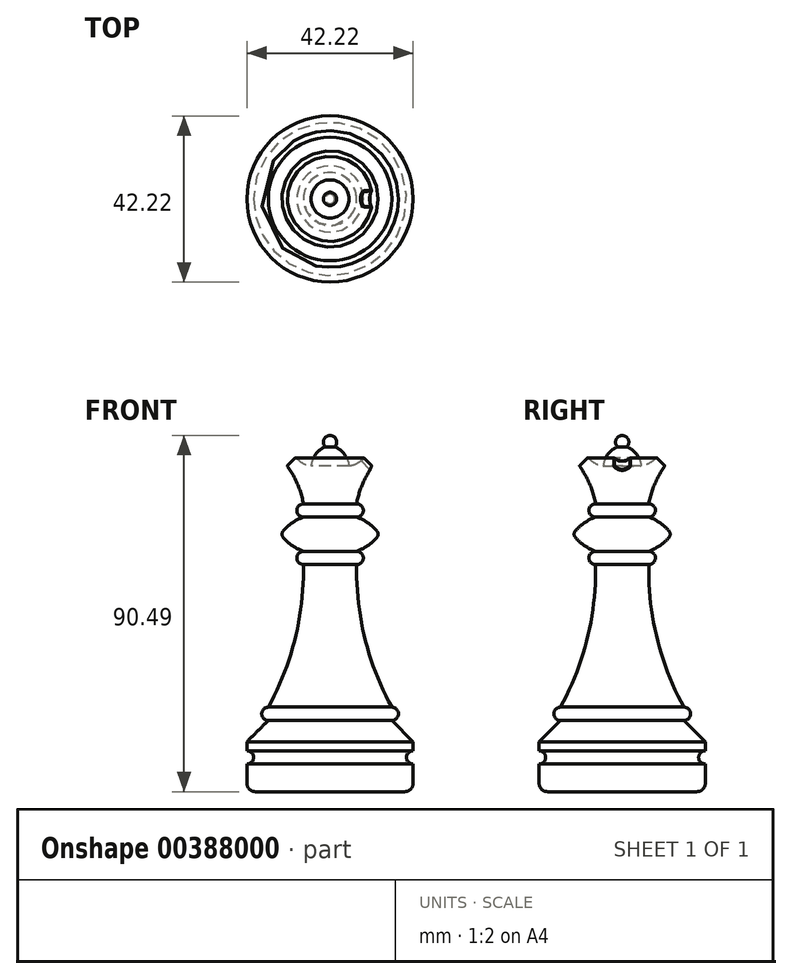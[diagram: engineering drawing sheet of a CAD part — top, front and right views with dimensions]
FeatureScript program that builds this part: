
annotation { "Feature Type Name" : "Feature", "Feature Type Description" : "" }
export const myFeature = defineFeature(function(context is Context, id is Id, definition is map)
    precondition{}
    {
        {
            var Q0;
            Q0=qCreatedBy(makeId("Front.planeOp"),FACE);
            var sketch = newSketch(context, id + "F0", { "sketchPlane" : qUnion([Q0])});
            skLineSegment(sketch, "E0", {"start": v(0, 0) * mm, "end": v(16.51, 0) * mm});
            skLineSegment(sketch, "E1", {"start": v(16.51, 0) * mm, "end": v(22.23, -5.71) * mm});
            skLineSegment(sketch, "E2", {"start": v(22.23, -5.71) * mm, "end": v(22.23, -8.1) * mm});
            skArc(sketch, "E3", {"start": v(22.23, -8.1) * mm, "mid": v(20.45, -9.88) * mm, "end": v(22.23, -11.66) * mm});
            skLineSegment(sketch, "E4", {"start": v(22.23, -11.66) * mm, "end": v(22.23, -19.05) * mm});
            skLineSegment(sketch, "E5", {"start": v(22.23, -19.05) * mm, "end": v(0, -19.05) * mm});
            skLineSegment(sketch, "E6", {"start": v(0, -19.05) * mm, "end": v(0, 0) * mm});
            skSolve(sketch);
        }
        {
            var Q0;
            Q0=makeQuery(id+"F0.imprint","IMPRINT",FACE,{"disambiguationData":[TD([[makeQuery(id+"F0.imprint","IMPRINT",EDGE,{"derivedFrom":sQuery(id+"F0.wireOp",EDGE,"E0")}),-1.0]])]});
            var Q1;
            Q1=sQuery(id+"F0.wireOp",EDGE,"E6");
            revolve(context, id + "F1", {"entities" : qUnion([Q0]), "axis" : qUnion([Q1]), "revolveType" : RevolveType.FULL});
        }
        {
            var Q0;
            Q0=qCreatedBy(makeId("Front.planeOp"),FACE);
            var sketch = newSketch(context, id + "F2", { "sketchPlane" : qUnion([Q0])});
            skLineSegment(sketch, "E7", {"start": v(0, 76.2) * mm, "end": v(0, 0) * mm});
            skLineSegment(sketch, "E8", {"start": v(0, 0) * mm, "end": v(16.51, 0) * mm});
            skArc(sketch, "E9", {"start": v(16.51, 0) * mm, "mid": v(18.29, 1.78) * mm, "end": v(16.51, 3.56) * mm});
            skArc(sketch, "E10", {"start": v(7.11, 41.68) * mm, "mid": v(9.31, 22) * mm, "end": v(16.51, 3.56) * mm});
            skArc(sketch, "E11", {"start": v(7.11, 41.68) * mm, "mid": v(8.9, 43.46) * mm, "end": v(7.11, 45.24) * mm});
            skArc(sketch, "E12", {"start": v(7.11, 45.24) * mm, "mid": v(10.51, 47.06) * mm, "end": v(13.2, 49.8) * mm});
            skArc(sketch, "E13", {"start": v(13.2, 49.8) * mm, "mid": v(10.51, 52.56) * mm, "end": v(7.11, 54.38) * mm});
            skArc(sketch, "E14", {"start": v(7.11, 54.38) * mm, "mid": v(8.9, 56.16) * mm, "end": v(7.11, 57.94) * mm});
            skArc(sketch, "E15", {"start": v(11.43, 68.1) * mm, "mid": v(8.71, 63.26) * mm, "end": v(7.11, 57.94) * mm});
            skLineSegment(sketch, "E16", {"start": v(11.43, 68.1) * mm, "end": v(9.18, 70.34) * mm});
            skArc(sketch, "E17", {"start": v(5.08, 68.1) * mm, "mid": v(7.35, 68.83) * mm, "end": v(9.18, 70.34) * mm});
            skArc(sketch, "E18", {"start": v(5.08, 68.1) * mm, "mid": v(3.86, 71.15) * mm, "end": v(1.27, 73.18) * mm});
            skArc(sketch, "E19", {"start": v(1.27, 73.18) * mm, "mid": v(1.64, 75.11) * mm, "end": v(0, 76.2) * mm});
            skLineSegment(sketch, "E20", {"start": v(7.11, 54.38) * mm, "end": v(7.11, 45.24) * mm, "construction": true});
            skLineSegment(sketch, "E21", {"start": v(13.2, 49.8) * mm, "end": v(7.11, 49.8) * mm, "construction": true});
            skSolve(sketch);
        }
        {
            var Q0;
            Q0=makeQuery(id+"F2.imprint","IMPRINT",FACE,{"disambiguationData":[TD([[makeQuery(id+"F2.imprint","IMPRINT",EDGE,{"derivedFrom":sQuery(id+"F2.wireOp",EDGE,"E7")}),1.0]])]});
            var Q1;
            Q1=sQuery(id+"F2.wireOp",EDGE,"E7");
            revolve(context, id + "F3", {"operationType" : NewBodyOperationType.ADD, "entities" : qUnion([Q0]), "axis" : qUnion([Q1]), "revolveType" : RevolveType.FULL});
        }
        {
            var Q0;
            Q0=sQuery(id+"F2.wireOp",VERTEX,"E15.start");
            var Q1;
            Q1=sQuery(id+"F2.wireOp",EDGE,"E16");
            cPlane(context, id + "F4", {"entities" : qUnion([Q0, Q1]), "cplaneType" : CPlaneType.LINE_POINT, "offset" : 25.4 * mm, "width" : 152.4 * mm, "height" : 152.4 * mm});
        }
        {
            var Q0;
            Q0=qCreatedBy(id+"F4.planeOp",FACE);
            var sketch = newSketch(context, id + "F5", { "sketchPlane" : qUnion([Q0])});
            skCircle(sketch, "E22", {"center": v(0, 57.5) * mm, "radius": 2.54 * mm});
            skSolve(sketch);
        }
        {
            var Q0;
            Q0 = qSketchRegion(id + "F5", true);
            extrude(context, id + "F6", {"entities" : qUnion([Q0]), "operationType" : NewBodyOperationType.REMOVE, "depth" : 5.08 * mm, "hasSecondDirection" : true, "secondDirectionOppositeDirection" : true, "secondDirectionDepth" : 5.08 * mm});
        }
        {
            var Q0;
            Q0=makeQuery(id+"F6.boolean.opBoolean","INTERSECT",EDGE,{"disambiguationData":[OD(1.0)],"derivedFrom":[makeQuery(id+"F3.opRevolve","SWEPT_FACE",FACE,{"disambiguationData":[OSD([sQuery(id+"F2.wireOp",EDGE,"E16")])]}),makeQuery(id+"F6.opExtrude","SWEPT_FACE",FACE,{"disambiguationData":[OSD([sQuery(id+"F5.wireOp",EDGE,"E22")])]})]});
            var Q1;
            Q1=makeQuery(id+"F6.boolean.opBoolean","INTERSECT",EDGE,{"disambiguationData":[OD(0.0)],"derivedFrom":[makeQuery(id+"F3.opRevolve","SWEPT_FACE",FACE,{"disambiguationData":[OSD([sQuery(id+"F2.wireOp",EDGE,"E16")])]}),makeQuery(id+"F6.opExtrude","SWEPT_FACE",FACE,{"disambiguationData":[OSD([sQuery(id+"F5.wireOp",EDGE,"E22")])]})]});
            fillet(context, id + "F7", {"entities" : qUnion([Q0, Q1]), "radius" : 0.2 * mm, "tangentPropagation" : true, "allowEdgeOverflow" : false});
        }
        {
            var Q0;
            Q0=makeQuery(id+"F6.boolean.opBoolean","INTERSECT",EDGE,{"derivedFrom":[makeQuery(id+"F3.opRevolve","SWEPT_FACE",FACE,{"disambiguationData":[OSD([sQuery(id+"F2.wireOp",EDGE,"E17")])]}),makeQuery(id+"F6.opExtrude","SWEPT_FACE",FACE,{"disambiguationData":[OSD([sQuery(id+"F5.wireOp",EDGE,"E22")])]})]});
            var Q1;
            Q1=makeQuery(id+"F6.boolean.opBoolean","INTERSECT",EDGE,{"derivedFrom":[makeQuery(id+"F3.opRevolve","SWEPT_FACE",FACE,{"disambiguationData":[OSD([sQuery(id+"F2.wireOp",EDGE,"E15")])]}),makeQuery(id+"F6.opExtrude","SWEPT_FACE",FACE,{"disambiguationData":[OSD([sQuery(id+"F5.wireOp",EDGE,"E22")])]})]});
            fillet(context, id + "F8", {"entities" : qUnion([Q0, Q1]), "radius" : 0.2 * mm, "tangentPropagation" : true, "allowEdgeOverflow" : false});
        }
        {
            var Q0;
            Q0=makeQuery(id+"F1.opRevolve","SWEPT_EDGE",EDGE,{"disambiguationData":[OSD([sQuery(id+"F0.wireOp",EDGE,"E4"),sQuery(id+"F0.wireOp",EDGE,"E5")])]});
            fillet(context, id + "F9", {"entities" : qUnion([Q0]), "radius" : 2.22 * mm, "tangentPropagation" : true, "defaultsChanged" : true, "vertexSettings" : [], "allowEdgeOverflow" : false});
        }
        {
            var Q0;
            Q0=makeQuery(id+"F1.opRevolve","SWEPT_BODY",BODY,{"disambiguationData":[OSD([sQuery(id+"F0.wireOp",EDGE,"E0"),sQuery(id+"F0.wireOp",EDGE,"E1"),sQuery(id+"F0.wireOp",EDGE,"E2"),sQuery(id+"F0.wireOp",EDGE,"E3"),sQuery(id+"F0.wireOp",EDGE,"E4"),sQuery(id+"F0.wireOp",EDGE,"E5"),sQuery(id+"F0.wireOp",EDGE,"E6")])]});
            var Q1;
            Q1=qCreatedBy(makeId("Origin.pointOp"),VERTEX);
            transform(context, id + "F10", {"entities" : qUnion([Q0]), "transformType" : TransformType.SCALE_UNIFORMLY, "scale" : .95, "scalePoint" : qUnion([Q1]), "makeCopy" : false});
        }
        {
            var Q0;
            Q0=makeQuery(id+"F3.opRevolve","SWEPT_EDGE",EDGE,{"disambiguationData":[OSD([sQuery(id+"F2.wireOp",EDGE,"E12"),sQuery(id+"F2.wireOp",EDGE,"E13")])]});
            fillet(context, id + "F11", {"entities" : qUnion([Q0]), "radius" : 1.27 * mm, "tangentPropagation" : true, "allowEdgeOverflow" : false});
        }
    });
